# Revit family: BDG_Boss Design_Stng_BOD-01 - Bodie - Armchair
name_source: partatom
category: Furniture
revit_build: Autodesk Revit 2017 (Build: 20160225_1515(x64)
units: mm (PartAtom-declared; Revit-internal decimal feet)

## family parameters
Always vertical = Yes
Cut with Voids When Loaded = No
OmniClass Number = 23.40.20.00
OmniClass Title = General Furniture and Specialties
Room Calculation Point = No
Shared = Yes
Work Plane-Based = Yes

## types (1)
- BDG_Boss Design_Stng_BOD-01 - Bodie - Armchair
    Base = BDG_Camira_Fabric_Blazer_MidnightBlue
    Default Elevation = 1219 mm
    Description = Bodie - Armchair
    Fire Rating = Standard BS5852 - Crib 5 Foams
    Manufacturer = Boss Design
    ManufacturerURL = https://www.bossdesign.com
    Model = BOD-01
    ModelNumber = BOD-01
    ModelReference = Bodie - Armchair
    NominalDepth = 850 mm
    NominalHeight = 760 mm
    NominalWidth = 960 mm
    Product Name = BOD-01 - Bodie - Armchair
    SeatHeight = 445 mm
    Size = 650 x 620 x 790mm
    Supplier = Lyndon
    URL = https://www.bossdesign.com

## geometry (parser evidence)
native form markers: Sweep x2
no freeform markers — native parametric forms only
